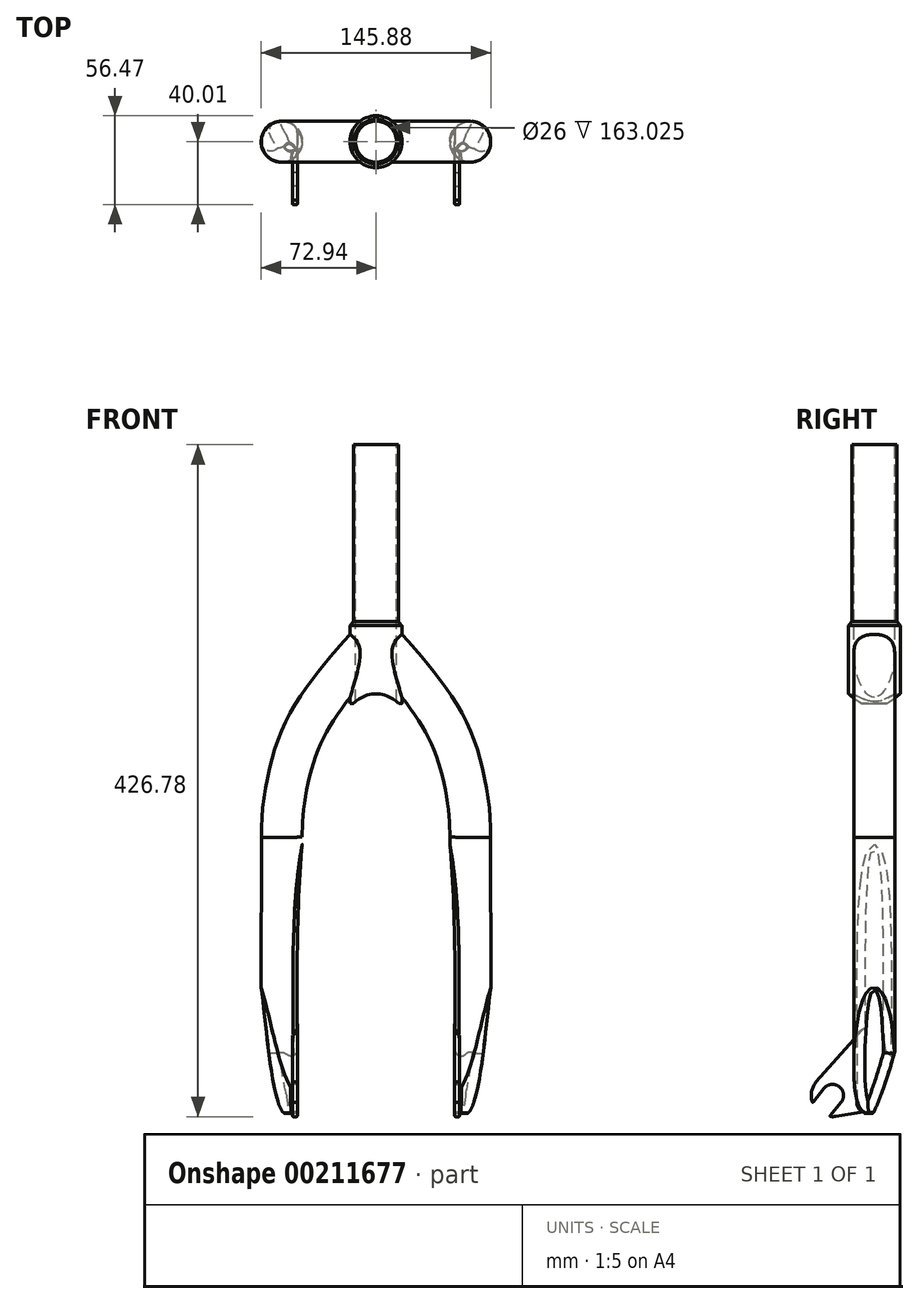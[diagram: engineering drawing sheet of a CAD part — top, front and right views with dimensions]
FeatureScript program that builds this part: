
annotation { "Feature Type Name" : "Feature", "Feature Type Description" : "" }
export const myFeature = defineFeature(function(context is Context, id is Id, definition is map)
    precondition{}
    {
        {
            var Q0;
            Q0=qCreatedBy(makeId("Top.planeOp"),FACE);
            var sketch = newSketch(context, id + "F0", { "sketchPlane" : qUnion([Q0])});
            skCircle(sketch, "E0", {"center": v(0, 0) * mm, "radius": 14.25 * mm});
            skSolve(sketch);
        }
        {
            var Q0;
            Q0 = qSketchRegion(id + "F0", true);
            extrude(context, id + "F1", {"entities" : qUnion([Q0]), "depth" : 162.4 * mm});
        }
        {
            var Q0;
            Q0=qCreatedBy(makeId("Front.planeOp"),FACE);
            var sketch = newSketch(context, id + "F2", { "sketchPlane" : qUnion([Q0])});
            skLineSegment(sketch, "E1", {"start": v(0, 0) * mm, "end": v(-14.25, 0) * mm});
            skLineSegment(sketch, "E2", {"start": v(-14.25, 0) * mm, "end": v(-16.46, -2.53) * mm});
            skLineSegment(sketch, "E3", {"start": v(0, 0) * mm, "end": v(0, -52) * mm});
            skLineSegment(sketch, "E4", {"start": v(0, -52) * mm, "end": v(-16.46, -52) * mm});
            skLineSegment(sketch, "E5", {"start": v(-16.46, -2.53) * mm, "end": v(-16.46, -52) * mm});
            skSolve(sketch);
        }
        {
            var Q0;
            Q0=makeQuery(id+"F2.imprint","IMPRINT",FACE,{"disambiguationData":[TD([[makeQuery(id+"F2.imprint","IMPRINT",EDGE,{"derivedFrom":sQuery(id+"F2.wireOp",EDGE,"E1")}),1.0]])]});
            var Q1;
            Q1=sQuery(id+"F2.wireOp",EDGE,"E3");
            revolve(context, id + "F3", {"operationType" : NewBodyOperationType.ADD, "entities" : qUnion([Q0]), "axis" : qUnion([Q1]), "revolveType" : RevolveType.FULL});
        }
        {
            var Q0;
            Q0=qCreatedBy(makeId("Front.planeOp"),FACE);
            var sketch = newSketch(context, id + "F4", { "sketchPlane" : qUnion([Q0])});
            skCircle(sketch, "E6", {"center": v(0, -65.82) * mm, "radius": 20 * mm});
            skSolve(sketch);
        }
        {
            var Q0;
            Q0=makeQuery(id+"F4.imprint","IMPRINT",FACE,{"disambiguationData":[TD([[makeQuery(id+"F4.imprint","IMPRINT",EDGE,{"derivedFrom":sQuery(id+"F4.wireOp",EDGE,"E6")}),1.0]])]});
            extrude(context, id + "F5", {"entities" : qUnion([Q0]), "depth" : 19 * mm, "hasSecondDirection" : true, "secondDirectionOppositeDirection" : true, "secondDirectionDepth" : 19.7 * mm});
        }
        {
            var Q0;
            Q0=makeQuery(id+"F5.opExtrude","SWEPT_BODY",BODY,{"disambiguationData":[OSD([sQuery(id+"F4.wireOp",EDGE,"E6")])]});
            var Q1;
            Q1=makeQuery(id+"F1.opExtrude","SWEPT_BODY",BODY,{"disambiguationData":[OSD([sQuery(id+"F0.wireOp",EDGE,"E0")])]});
            booleanBodies(context, id + "F6", {"operationType" : BooleanOperationType.SUBTRACTION, "tools" : qUnion([Q0]), "targets" : qUnion([Q1])});
        }
        {
            var Q0;
            Q0=qCreatedBy(makeId("Top.planeOp"),FACE);
            cPlane(context, id + "F7", {"entities" : qUnion([Q0]), "cplaneType" : CPlaneType.OFFSET, "offset" : 315 * mm, "oppositeDirection" : true, "width" : 150 * mm, "height" : 150 * mm});
        }
        {
            var Q0;
            Q0=qCreatedBy(id+"F7.planeOp",FACE);
            var sketch = newSketch(context, id + "F8", { "sketchPlane" : qUnion([Q0])});
            skCircle(sketch, "E7", {"center": v(-60, 0) * mm, "radius": 13 * mm});
            skLineSegment(sketch, "E8", {"start": v(0, 0) * mm, "end": v(-60, 0) * mm});
            skSolve(sketch);
        }
        {
            var Q0;
            Q0=qCreatedBy(makeId("Front.planeOp"),FACE);
            var sketch = newSketch(context, id + "F9", { "sketchPlane" : qUnion([Q0])});
            skPoint(sketch, "E9.0", {"position": v(-60, -315) * mm});
            skFitSpline(sketch, "E10", {"points": [v(0, -8.9) * mm, v(-47.93, -74.33) * mm, v(-59.86, -136.93) * mm], "startDerivative": vector(-113.13, -130.43) * mm, "endDerivative": vector(1.5, -99.2) * mm});
            skLineSegment(sketch, "E11", {"start": v(-60, -315) * mm, "end": v(-59.86, -136.93) * mm});
            skSolve(sketch);
        }
        {
            var Q0;
            Q0=makeQuery(id+"F8.imprint","IMPRINT",FACE,{"disambiguationData":[TD([[makeQuery(id+"F8.imprint","IMPRINT",EDGE,{"derivedFrom":sQuery(id+"F8.wireOp",EDGE,"E7")}),1.0]])]});
            var Q1;
            Q1=sQuery(id+"F9.wireOp",EDGE,"E11");
            var Q2;
            Q2=sQuery(id+"F9.wireOp",EDGE,"E10");
            sweep(context, id + "F10", {"operationType" : NewBodyOperationType.ADD, "profiles" : qUnion([Q0]), "path" : qUnion([Q1, Q2])});
        }
        {
            var Q0;
            Q0=makeQuery(id+"F1.opExtrude","SWEPT_BODY",BODY,{"disambiguationData":[OSD([sQuery(id+"F0.wireOp",EDGE,"E0")])]});
            var Q1;
            Q1=qCreatedBy(makeId("Right.planeOp"),FACE);
            mirror(context, id + "F11", {"operationType" : NewBodyOperationType.ADD, "entities" : qUnion([Q0]), "mirrorPlane" : qUnion([Q1])});
        }
        {
            var Q0;
            Q0=makeQuery(id+"F1.opExtrude","CAP_FACE",FACE,{"disambiguationData":[OSD([sQuery(id+"F0.wireOp",EDGE,"E0")])],"isStart":false});
            var sketch = newSketch(context, id + "F12", { "sketchPlane" : qUnion([Q0])});
            skCircle(sketch, "E12", {"center": v(0, 0) * mm, "radius": 13 * mm});
            skSolve(sketch);
        }
        {
            var Q0;
            Q0=makeQuery(id+"F12.imprint","IMPRINT",FACE,{"disambiguationData":[TD([[makeQuery(id+"F12.imprint","IMPRINT",EDGE,{"derivedFrom":sQuery(id+"F12.wireOp",EDGE,"E12")}),1.0]])]});
            var Q1;
            Q1=sQuery(id+"F12.wireOp",EDGE,"E12");
            extrude(context, id + "F13", {"entities" : qUnion([Q0]), "operationType" : NewBodyOperationType.REMOVE, "surfaceEntities" : qUnion([Q1]), "oppositeDirection" : true, "depth" : 243.5 * mm});
        }
        {
            var Q0;
            Q0=makeQuery(id+"F10.boolean.opBoolean","INTERSECT",EDGE,{"derivedFrom":[makeQuery(id+"F3.opRevolve","SWEPT_FACE",FACE,{"disambiguationData":[OSD([sQuery(id+"F2.wireOp",EDGE,"E5")])]}),makeQuery(id+"F10.opSweep","SWEPT_FACE",FACE,{"disambiguationData":[OSD([sQuery(id+"F8.wireOp",EDGE,"E7"),sQuery(id+"F9.wireOp",EDGE,"E10")])]})]});
            var Q1;
            Q1=makeQuery(id+"F11.opPattern","COPY",EDGE,{"derivedFrom":makeQuery(id+"F10.boolean.opBoolean","INTERSECT",EDGE,{"derivedFrom":[makeQuery(id+"F3.opRevolve","SWEPT_FACE",FACE,{"disambiguationData":[OSD([sQuery(id+"F2.wireOp",EDGE,"E5")])]}),makeQuery(id+"F10.opSweep","SWEPT_FACE",FACE,{"disambiguationData":[OSD([sQuery(id+"F8.wireOp",EDGE,"E7"),sQuery(id+"F9.wireOp",EDGE,"E10")])]})]}),"instanceName":"1"});
            fillet(context, id + "F14", {"entities" : qUnion([Q0, Q1]), "radius" : 1 * mm, "tangentPropagation" : true, "allowEdgeOverflow" : false});
        }
        {
            var Q0;
            Q0=qCreatedBy(makeId("Right.planeOp"),FACE);
            var sketch = newSketch(context, id + "F15", { "sketchPlane" : qUnion([Q0])});
            skArc(sketch, "E13", {"start": v(-37, -292.37) * mm, "mid": v(-38.2, -307.64) * mm, "end": v(-24.36, -314.2) * mm});
            skLineSegment(sketch, "E14", {"start": v(0, -250.54) * mm, "end": v(0, -310.31) * mm});
            skLineSegment(sketch, "E15", {"start": v(-24.36, -314.2) * mm, "end": v(0, -310.31) * mm});
            skLineSegment(sketch, "E16", {"start": v(-37, -292.37) * mm, "end": v(0, -250.54) * mm});
            skSolve(sketch);
        }
        {
            var Q0;
            Q0=makeQuery(id+"F15.imprint","IMPRINT",FACE,{"disambiguationData":[TD([[makeQuery(id+"F15.imprint","IMPRINT",EDGE,{"derivedFrom":sQuery(id+"F15.wireOp",EDGE,"E13")}),1.0]])]});
            extrude(context, id + "F16", {"entities" : qUnion([Q0]), "operationType" : NewBodyOperationType.ADD, "depth" : 53 * mm, "hasSecondDirection" : true, "secondDirectionOppositeDirection" : true, "secondDirectionDepth" : 53 * mm});
        }
        {
            var Q0;
            Q0=qCreatedBy(makeId("Right.planeOp"),FACE);
            var sketch = newSketch(context, id + "F17", { "sketchPlane" : qUnion([Q0])});
            skLineSegment(sketch, "E17.0.1", {"start": v(-10.96, -312.06) * mm, "end": v(-24.36, -314.2) * mm});
            skArc(sketch, "E17.0.2", {"start": v(-24.36, -314.2) * mm, "mid": v(-38.2, -307.64) * mm, "end": v(-37, -292.37) * mm});
            skLineSegment(sketch, "E17.0.3", {"start": v(-37, -292.37) * mm, "end": v(-10.98, -262.96) * mm});
            skLineSegment(sketch, "E18", {"start": v(-37, -292.37) * mm, "end": v(17.67, -230.56) * mm});
            skLineSegment(sketch, "E19", {"start": v(-24.36, -314.2) * mm, "end": v(43.27, -303.4) * mm});
            skLineSegment(sketch, "E20", {"start": v(43.27, -303.4) * mm, "end": v(17.67, -230.56) * mm});
            skSolve(sketch);
        }
        {
            var Q0;
            Q0 = qSketchRegion(id + "F17", true);
            extrude(context, id + "F18", {"entities" : qUnion([Q0]), "operationType" : NewBodyOperationType.REMOVE, "oppositeDirection" : true, "depth" : 50 * mm, "hasSecondDirection" : true, "secondDirectionOppositeDirection" : false, "secondDirectionDepth" : 50 * mm});
        }
        {
            var Q0;
            Q0=makeQuery(id+"F10.opSweep","CAP_FACE",FACE,{"disambiguationData":[OSD([sQuery(id+"F8.wireOp",EDGE,"E7"),sQuery(id+"F9.wireOp",VERTEX,"E11.start")])],"isStart":true});
            var sketch = newSketch(context, id + "F19", { "sketchPlane" : qUnion([Q0])});
            skCircle(sketch, "E21", {"center": v(-60, 0) * mm, "radius": 13.5 * mm});
            skSolve(sketch);
        }
        {
            var Q0;
            Q0 = qSketchRegion(id + "F19", true);
            extrude(context, id + "F20", {"entities" : qUnion([Q0]), "operationType" : NewBodyOperationType.REMOVE, "oppositeDirection" : true, "depth" : 2.8 * mm});
        }
        {
            var Q0;
            Q0=makeQuery(id+"F1.opExtrude","SWEPT_BODY",BODY,{"disambiguationData":[OSD([sQuery(id+"F0.wireOp",EDGE,"E0")])]});
            var Q1;
            Q1=qCreatedBy(makeId("Right.planeOp"),FACE);
            mirror(context, id + "F21", {"operationType" : NewBodyOperationType.INTERSECT, "entities" : qUnion([Q0]), "mirrorPlane" : qUnion([Q1])});
        }
        {
            var Q0;
            Q0=qCreatedBy(makeId("Front.planeOp"),FACE);
            var sketch = newSketch(context, id + "F22", { "sketchPlane" : qUnion([Q0])});
            skFitSpline(sketch, "E22.0", {"points": [v(-47, -312.2) * mm, v(-55.66, -312.2) * mm, v(-64.33, -312.2) * mm, v(-73, -312.2) * mm]});
            skFitSpline(sketch, "E23", {"points": [v(-54.32, -320.93) * mm, v(-67.6, -277.9) * mm, v(-79.55, -201.3) * mm], "startDerivative": vector(-50.6, 60.55) * mm, "endDerivative": vector(-36.25, 107.2) * mm});
            skLineSegment(sketch, "E24", {"start": v(-54.32, -320.93) * mm, "end": v(-140.96, -341.08) * mm});
            skLineSegment(sketch, "E25", {"start": v(-140.96, -341.08) * mm, "end": v(-79.55, -201.3) * mm});
            skSolve(sketch);
        }
        {
            var Q0;
            {var subQ0=sQuery(id+"F22.wireOp",EDGE,"E24");Q0=makeQuery(id+"F22.imprint","IMPRINT",FACE,{"disambiguationData":[TD([[makeQuery(id+"F22.imprint","IMPRINT",EDGE,{"derivedFrom":subQ0}),-1.0]])]});}
            extrude(context, id + "F23", {"entities" : qUnion([Q0]), "operationType" : NewBodyOperationType.REMOVE, "oppositeDirection" : true, "depth" : 25 * mm, "hasSecondDirection" : true, "secondDirectionOppositeDirection" : false, "secondDirectionDepth" : 76.3 * mm});
        }
        {
            var Q0;
            Q0=qCreatedBy(makeId("Right.planeOp"),FACE);
            var sketch = newSketch(context, id + "F24", { "sketchPlane" : qUnion([Q0])});
            skFitSpline(sketch, "E26", {"points": [v(20.3, -244.57) * mm, v(11.96, -277) * mm, v(-12.12, -335.12) * mm, v(-46.63, -372.17) * mm], "startDerivative": vector(-24.7, -105.88) * mm, "endDerivative": vector(-108.24, -94.52) * mm});
            skLineSegment(sketch, "E27", {"start": v(20.3, -244.57) * mm, "end": v(48.1, -363.6) * mm});
            skLineSegment(sketch, "E28", {"start": v(48.1, -363.6) * mm, "end": v(-46.63, -372.17) * mm});
            skSolve(sketch);
        }
        {
            var Q0;
            Q0=makeQuery(id+"F24.imprint","IMPRINT",FACE,{"disambiguationData":[TD([[makeQuery(id+"F24.imprint","IMPRINT",EDGE,{"derivedFrom":sQuery(id+"F24.wireOp",EDGE,"E26")}),1.0]])]});
            extrude(context, id + "F25", {"entities" : qUnion([Q0]), "operationType" : NewBodyOperationType.REMOVE, "oppositeDirection" : true, "depth" : 92.1 * mm});
        }
        {
            var Q0;
            Q0=qCreatedBy(makeId("Front.planeOp"),FACE);
            var sketch = newSketch(context, id + "F26", { "sketchPlane" : qUnion([Q0])});
            skPoint(sketch, "E29.0", {"position": v(-50, -314.2) * mm});
            skLineSegment(sketch, "E30", {"start": v(-50, -314.2) * mm, "end": v(-50, -345.46) * mm});
            skLineSegment(sketch, "E31", {"start": v(-50, -314.2) * mm, "end": v(-50, -258.24) * mm});
            skFitSpline(sketch, "E32", {"points": [v(-50, -258.24) * mm, v(-50, -209.78) * mm, v(-46.14, -135.31) * mm, v(-36.08, -84.53) * mm], "startDerivative": vector(-1.03, 147.16) * mm, "endDerivative": vector(36.5, 149.52) * mm});
            skLineSegment(sketch, "E33", {"start": v(-36.08, -84.53) * mm, "end": v(-4.07, -180.95) * mm});
            skLineSegment(sketch, "E34", {"start": v(-4.07, -180.95) * mm, "end": v(-50, -345.46) * mm});
            skSolve(sketch);
        }
        {
            var Q0;
            Q0=makeQuery(id+"F26.imprint","IMPRINT",FACE,{"disambiguationData":[TD([[makeQuery(id+"F26.imprint","IMPRINT",EDGE,{"derivedFrom":sQuery(id+"F26.wireOp",EDGE,"E30")}),1.0]])]});
            extrude(context, id + "F27", {"entities" : qUnion([Q0]), "operationType" : NewBodyOperationType.REMOVE, "oppositeDirection" : true, "depth" : 164.6 * mm, "hasSecondDirection" : true, "secondDirectionOppositeDirection" : false, "secondDirectionDepth" : 151.8 * mm});
        }
        {
            var Q0;
            Q0=makeQuery(id+"F27.boolean.opBoolean","INTERSECT",EDGE,{"derivedFrom":[makeQuery(id+"F10.opSweep","SWEPT_FACE",FACE,{"disambiguationData":[OSD([sQuery(id+"F8.wireOp",EDGE,"E7"),sQuery(id+"F9.wireOp",EDGE,"E11")])]}),makeQuery(id+"F27.opExtrude","SWEPT_FACE",FACE,{"disambiguationData":[OSD([sQuery(id+"F26.wireOp",EDGE,"E32")])]})]});
            fillet(context, id + "F28", {"entities" : qUnion([Q0]), "radius" : 6 * mm, "tangentPropagation" : true, "allowEdgeOverflow" : false});
        }
        {
            var Q0;
            Q0=makeQuery(id+"F23.boolean.opBoolean","INTERSECT",EDGE,{"derivedFrom":[makeQuery(id+"F10.opSweep","SWEPT_FACE",FACE,{"disambiguationData":[OSD([sQuery(id+"F8.wireOp",EDGE,"E7"),sQuery(id+"F9.wireOp",EDGE,"E11")])]}),makeQuery(id+"F23.opExtrude","SWEPT_FACE",FACE,{"disambiguationData":[OSD([sQuery(id+"F22.wireOp",EDGE,"E23")])]})]});
            var Q1;
            Q1=makeQuery(id+"F25.boolean.opBoolean","INTERSECT",EDGE,{"derivedFrom":[makeQuery(id+"F23.boolean.opBoolean","COPY",FACE,{"derivedFrom":makeQuery(id+"F23.opExtrude","SWEPT_FACE",FACE,{"disambiguationData":[OSD([sQuery(id+"F22.wireOp",EDGE,"E23")])]})}),makeQuery(id+"F25.opExtrude","SWEPT_FACE",FACE,{"disambiguationData":[OSD([sQuery(id+"F24.wireOp",EDGE,"E26")])]})]});
            var Q2;
            Q2=makeQuery(id+"F27.boolean.opBoolean","INTERSECT",EDGE,{"derivedFrom":[makeQuery(id+"F25.boolean.opBoolean","COPY",FACE,{"derivedFrom":makeQuery(id+"F25.opExtrude","SWEPT_FACE",FACE,{"disambiguationData":[OSD([sQuery(id+"F24.wireOp",EDGE,"E26")])]})}),makeQuery(id+"F27.opExtrude","SWEPT_FACE",FACE,{"disambiguationData":[OSD([sQuery(id+"F26.wireOp",EDGE,"E30"),sQuery(id+"F26.wireOp",EDGE,"E31")])]})]});
            fillet(context, id + "F29", {"entities" : qUnion([Q0, Q1, Q2]), "radius" : 7 * mm, "tangentPropagation" : true, "allowEdgeOverflow" : false});
        }
        {
            var Q0;
            Q0=makeQuery(id+"F16.opExtrude","CAP_EDGE",EDGE,{"disambiguationData":[OSD([sQuery(id+"F15.wireOp",EDGE,"E15")])],"isStart":true});
            var Q1;
            {var subQ0=sQuery(id+"F17.wireOp",EDGE,"E19");Q1=makeQuery(id+"F18.boolean.opBoolean","COPY",EDGE,{"disambiguationData":[TD([makeQuery(id+"F10.opSweep","SWEPT_FACE",FACE,{"disambiguationData":[OSD([sQuery(id+"F8.wireOp",EDGE,"E7"),sQuery(id+"F9.wireOp",EDGE,"E11")])]}),makeQuery(id+"F16.opExtrude","SWEPT_FACE",FACE,{"disambiguationData":[OSD([sQuery(id+"F15.wireOp",EDGE,"E13")])]}),makeQuery(id+"F16.opExtrude","SWEPT_FACE",FACE,{"disambiguationData":[OSD([sQuery(id+"F15.wireOp",EDGE,"E15")])]}),makeQuery(id+"F18.opExtrude","CAP_FACE",FACE,{"disambiguationData":[OSD([sQuery(id+"F17.wireOp",EDGE,"E17.0.2"),sQuery(id+"F17.wireOp",EDGE,"E18"),subQ0,sQuery(id+"F17.wireOp",EDGE,"E20")])],"isStart":false}),makeQuery(id+"F18.opExtrude","SWEPT_FACE",FACE,{"disambiguationData":[OSD([subQ0])]})])],"derivedFrom":makeQuery(id+"F18.opExtrude","CAP_EDGE",EDGE,{"disambiguationData":[OSD([subQ0])],"isStart":false})});}
            var Q2;
            Q2=makeQuery(id+"F16.opExtrude","CAP_EDGE",EDGE,{"disambiguationData":[OSD([sQuery(id+"F15.wireOp",EDGE,"E13")])],"isStart":true});
            var Q3;
            Q3=makeQuery(id+"F18.boolean.opBoolean","COPY",EDGE,{"derivedFrom":makeQuery(id+"F18.opExtrude","CAP_EDGE",EDGE,{"disambiguationData":[OSD([sQuery(id+"F17.wireOp",EDGE,"E17.0.2")])],"isStart":false})});
            var Q4;
            Q4=makeQuery(id+"F16.opExtrude","CAP_EDGE",EDGE,{"disambiguationData":[OSD([sQuery(id+"F15.wireOp",EDGE,"E16")])],"isStart":true});
            var Q5;
            {var subQ0=sQuery(id+"F17.wireOp",EDGE,"E18");Q5=makeQuery(id+"F18.boolean.opBoolean","COPY",EDGE,{"disambiguationData":[TD([makeQuery(id+"F10.opSweep","SWEPT_FACE",FACE,{"disambiguationData":[OSD([sQuery(id+"F8.wireOp",EDGE,"E7"),sQuery(id+"F9.wireOp",EDGE,"E11")])]}),makeQuery(id+"F16.opExtrude","SWEPT_FACE",FACE,{"disambiguationData":[OSD([sQuery(id+"F15.wireOp",EDGE,"E13")])]}),makeQuery(id+"F16.opExtrude","SWEPT_FACE",FACE,{"disambiguationData":[OSD([sQuery(id+"F15.wireOp",EDGE,"E16")])]}),makeQuery(id+"F18.opExtrude","CAP_FACE",FACE,{"disambiguationData":[OSD([sQuery(id+"F17.wireOp",EDGE,"E17.0.2"),subQ0,sQuery(id+"F17.wireOp",EDGE,"E19"),sQuery(id+"F17.wireOp",EDGE,"E20")])],"isStart":false}),makeQuery(id+"F18.opExtrude","SWEPT_FACE",FACE,{"disambiguationData":[OSD([subQ0])]})])],"derivedFrom":makeQuery(id+"F18.opExtrude","CAP_EDGE",EDGE,{"disambiguationData":[OSD([subQ0])],"isStart":false})});}
            fillet(context, id + "F30", {"entities" : qUnion([Q0, Q1, Q2, Q3, Q4, Q5]), "radius" : .5 * mm, "tangentPropagation" : true, "allowEdgeOverflow" : false});
        }
        {
            var Q0;
            Q0=makeQuery(id+"F29.opFillet","BLEND_EDGE",EDGE,{"disambiguationData":[OD(1.0)],"blendedFrom":[makeQuery(id+"F27.boolean.opBoolean","INTERSECT",EDGE,{"derivedFrom":[makeQuery(id+"F25.boolean.opBoolean","COPY",FACE,{"derivedFrom":makeQuery(id+"F25.opExtrude","SWEPT_FACE",FACE,{"disambiguationData":[OSD([sQuery(id+"F24.wireOp",EDGE,"E26")])]})}),makeQuery(id+"F27.opExtrude","SWEPT_FACE",FACE,{"disambiguationData":[OSD([sQuery(id+"F26.wireOp",EDGE,"E30"),sQuery(id+"F26.wireOp",EDGE,"E31")])]})]}),makeQuery(id+"F20.boolean.opBoolean","COPY",FACE,{"derivedFrom":makeQuery(id+"F20.opExtrude","CAP_FACE",FACE,{"disambiguationData":[OSD([sQuery(id+"F19.wireOp",EDGE,"E21")])],"isStart":false})})],"blendedInto":[makeQuery(id+"F20.boolean.opBoolean","COPY",FACE,{"derivedFrom":makeQuery(id+"F20.opExtrude","CAP_FACE",FACE,{"disambiguationData":[OSD([sQuery(id+"F19.wireOp",EDGE,"E21")])],"isStart":false})})]});
            var Q1;
            Q1=makeQuery(id+"F29.opFillet","BLEND_EDGE",EDGE,{"disambiguationData":[OD(0.0)],"blendedFrom":[makeQuery(id+"F27.boolean.opBoolean","INTERSECT",EDGE,{"derivedFrom":[makeQuery(id+"F25.boolean.opBoolean","COPY",FACE,{"derivedFrom":makeQuery(id+"F25.opExtrude","SWEPT_FACE",FACE,{"disambiguationData":[OSD([sQuery(id+"F24.wireOp",EDGE,"E26")])]})}),makeQuery(id+"F27.opExtrude","SWEPT_FACE",FACE,{"disambiguationData":[OSD([sQuery(id+"F26.wireOp",EDGE,"E30"),sQuery(id+"F26.wireOp",EDGE,"E31")])]})]}),makeQuery(id+"F20.boolean.opBoolean","COPY",FACE,{"derivedFrom":makeQuery(id+"F20.opExtrude","CAP_FACE",FACE,{"disambiguationData":[OSD([sQuery(id+"F19.wireOp",EDGE,"E21")])],"isStart":false})})],"blendedInto":[makeQuery(id+"F20.boolean.opBoolean","COPY",FACE,{"derivedFrom":makeQuery(id+"F20.opExtrude","CAP_FACE",FACE,{"disambiguationData":[OSD([sQuery(id+"F19.wireOp",EDGE,"E21")])],"isStart":false})})]});
            var Q2;
            Q2=makeQuery(id+"F29.opFillet","BLEND_EDGE",EDGE,{"disambiguationData":[OD(1.0)],"blendedFrom":[makeQuery(id+"F25.boolean.opBoolean","INTERSECT",EDGE,{"derivedFrom":[makeQuery(id+"F23.boolean.opBoolean","COPY",FACE,{"derivedFrom":makeQuery(id+"F23.opExtrude","SWEPT_FACE",FACE,{"disambiguationData":[OSD([sQuery(id+"F22.wireOp",EDGE,"E23")])]})}),makeQuery(id+"F25.opExtrude","SWEPT_FACE",FACE,{"disambiguationData":[OSD([sQuery(id+"F24.wireOp",EDGE,"E26")])]})]}),makeQuery(id+"F20.boolean.opBoolean","COPY",FACE,{"derivedFrom":makeQuery(id+"F20.opExtrude","CAP_FACE",FACE,{"disambiguationData":[OSD([sQuery(id+"F19.wireOp",EDGE,"E21")])],"isStart":false})})],"blendedInto":[makeQuery(id+"F20.boolean.opBoolean","COPY",FACE,{"derivedFrom":makeQuery(id+"F20.opExtrude","CAP_FACE",FACE,{"disambiguationData":[OSD([sQuery(id+"F19.wireOp",EDGE,"E21")])],"isStart":false})})]});
            var Q3;
            Q3=makeQuery(id+"F29.opFillet","BLEND_EDGE",EDGE,{"disambiguationData":[OD(0.0)],"blendedFrom":[makeQuery(id+"F25.boolean.opBoolean","INTERSECT",EDGE,{"derivedFrom":[makeQuery(id+"F23.boolean.opBoolean","COPY",FACE,{"derivedFrom":makeQuery(id+"F23.opExtrude","SWEPT_FACE",FACE,{"disambiguationData":[OSD([sQuery(id+"F22.wireOp",EDGE,"E23")])]})}),makeQuery(id+"F25.opExtrude","SWEPT_FACE",FACE,{"disambiguationData":[OSD([sQuery(id+"F24.wireOp",EDGE,"E26")])]})]}),makeQuery(id+"F20.boolean.opBoolean","COPY",FACE,{"derivedFrom":makeQuery(id+"F20.opExtrude","CAP_FACE",FACE,{"disambiguationData":[OSD([sQuery(id+"F19.wireOp",EDGE,"E21")])],"isStart":false})})],"blendedInto":[makeQuery(id+"F20.boolean.opBoolean","COPY",FACE,{"derivedFrom":makeQuery(id+"F20.opExtrude","CAP_FACE",FACE,{"disambiguationData":[OSD([sQuery(id+"F19.wireOp",EDGE,"E21")])],"isStart":false})})]});
            var Q4;
            Q4=makeQuery(id+"F29.opFillet","BLEND_EDGE",EDGE,{"blendedFrom":[makeQuery(id+"F23.boolean.opBoolean","INTERSECT",EDGE,{"derivedFrom":[makeQuery(id+"F10.opSweep","SWEPT_FACE",FACE,{"disambiguationData":[OSD([sQuery(id+"F8.wireOp",EDGE,"E7"),sQuery(id+"F9.wireOp",EDGE,"E11")])]}),makeQuery(id+"F23.opExtrude","SWEPT_FACE",FACE,{"disambiguationData":[OSD([sQuery(id+"F22.wireOp",EDGE,"E23")])]})]}),makeQuery(id+"F20.boolean.opBoolean","COPY",FACE,{"derivedFrom":makeQuery(id+"F20.opExtrude","CAP_FACE",FACE,{"disambiguationData":[OSD([sQuery(id+"F19.wireOp",EDGE,"E21")])],"isStart":false})})],"blendedInto":[makeQuery(id+"F20.boolean.opBoolean","COPY",FACE,{"derivedFrom":makeQuery(id+"F20.opExtrude","CAP_FACE",FACE,{"disambiguationData":[OSD([sQuery(id+"F19.wireOp",EDGE,"E21")])],"isStart":false})})]});
            var Q5;
            Q5=makeQuery(id+"F20.boolean.opBoolean","INTERSECT",EDGE,{"derivedFrom":[makeQuery(id+"F10.opSweep","SWEPT_FACE",FACE,{"disambiguationData":[OSD([sQuery(id+"F8.wireOp",EDGE,"E7"),sQuery(id+"F9.wireOp",EDGE,"E11")])]}),makeQuery(id+"F20.opExtrude","CAP_FACE",FACE,{"disambiguationData":[OSD([sQuery(id+"F19.wireOp",EDGE,"E21")])],"isStart":false})]});
            var Q6;
            Q6=makeQuery(id+"F27.boolean.opBoolean","INTERSECT",EDGE,{"derivedFrom":[makeQuery(id+"F20.boolean.opBoolean","COPY",FACE,{"derivedFrom":makeQuery(id+"F20.opExtrude","CAP_FACE",FACE,{"disambiguationData":[OSD([sQuery(id+"F19.wireOp",EDGE,"E21")])],"isStart":false})}),makeQuery(id+"F27.opExtrude","SWEPT_FACE",FACE,{"disambiguationData":[OSD([sQuery(id+"F26.wireOp",EDGE,"E30"),sQuery(id+"F26.wireOp",EDGE,"E31")])]})]});
            fillet(context, id + "F31", {"entities" : qUnion([Q0, Q1, Q2, Q3, Q4, Q5, Q6]), "radius" : 1 * mm, "tangentPropagation" : true, "allowEdgeOverflow" : false});
        }
        {
            var Q0;
            Q0=makeQuery(id+"F16.boolean.opBoolean","INTERSECT",EDGE,{"derivedFrom":[makeQuery(id+"F10.opSweep","SWEPT_FACE",FACE,{"disambiguationData":[OSD([sQuery(id+"F8.wireOp",EDGE,"E7"),sQuery(id+"F9.wireOp",EDGE,"E11")])]}),makeQuery(id+"F16.opExtrude","CAP_FACE",FACE,{"disambiguationData":[OSD([sQuery(id+"F15.wireOp",EDGE,"E13"),sQuery(id+"F15.wireOp",EDGE,"E14"),sQuery(id+"F15.wireOp",EDGE,"E15"),sQuery(id+"F15.wireOp",EDGE,"E16")])],"isStart":true})]});
            fillet(context, id + "F32", {"entities" : qUnion([Q0]), "radius" : 1 * mm, "tangentPropagation" : true, "allowEdgeOverflow" : false});
        }
        {
            var Q0;
            Q0=makeQuery(id+"F1.opExtrude","SWEPT_BODY",BODY,{"disambiguationData":[OSD([sQuery(id+"F0.wireOp",EDGE,"E0")])]});
            var Q1;
            Q1=qCreatedBy(makeId("Right.planeOp"),FACE);
            mirror(context, id + "F33", {"operationType" : NewBodyOperationType.INTERSECT, "entities" : qUnion([Q0]), "mirrorPlane" : qUnion([Q1])});
        }
        {
            var Q0;
            {var subQ0=sQuery(id+"F15.wireOp",EDGE,"E16");var subQ1=sQuery(id+"F15.wireOp",EDGE,"E15");var subQ2=sQuery(id+"F15.wireOp",EDGE,"E14");var subQ3=sQuery(id+"F15.wireOp",EDGE,"E13");Q0=makeQuery(id+"F33.boolean.opBoolean","MERGE",FACE,{"derivedFrom":[makeQuery(id+"F16.opExtrude","CAP_FACE",FACE,{"disambiguationData":[OSD([subQ3,subQ2,subQ1,subQ0])],"isStart":true}),makeQuery(id+"F33.boolean.toolComplement.opBoolean","COPY",FACE,{"derivedFrom":makeQuery(id+"F33.opPattern","COPY",FACE,{"derivedFrom":makeQuery(id+"F16.opExtrude","CAP_FACE",FACE,{"disambiguationData":[OSD([subQ3,subQ2,subQ1,subQ0])],"isStart":false}),"instanceName":"1"})})]});}
            var sketch = newSketch(context, id + "F34", { "sketchPlane" : qUnion([Q0])});
            skLineSegment(sketch, "E35", {"start": v(21.08, -305.29) * mm, "end": v(30.46, -316.86) * mm});
            skLineSegment(sketch, "E36", {"start": v(30.46, -316.86) * mm, "end": v(41.34, -308.04) * mm});
            skArc(sketch, "E37", {"start": v(21.08, -305.29) * mm, "mid": v(22.1, -295.44) * mm, "end": v(31.95, -296.47) * mm});
            skLineSegment(sketch, "E38", {"start": v(41.34, -308.04) * mm, "end": v(31.95, -296.47) * mm});
            skSolve(sketch);
        }
        {
            var Q0;
            Q0 = qSketchRegion(id + "F34", true);
            extrude(context, id + "F35", {"entities" : qUnion([Q0]), "operationType" : NewBodyOperationType.REMOVE, "oppositeDirection" : true, "depth" : 25 * mm});
        }
        {
            var Q0;
            {var subQ0=sQuery(id+"F15.wireOp",EDGE,"E16");var subQ1=sQuery(id+"F15.wireOp",EDGE,"E15");var subQ2=sQuery(id+"F15.wireOp",EDGE,"E13");Q0=makeQuery(id+"F35.boolean.opBoolean","INTERSECT",EDGE,{"derivedFrom":[makeQuery(id+"F18.boolean.opBoolean","SPLIT",FACE,{"disambiguationData":[TD([makeQuery(id+"F16.opExtrude","CAP_FACE",FACE,{"disambiguationData":[OSD([subQ2,sQuery(id+"F15.wireOp",EDGE,"E14"),subQ1,subQ0])],"isStart":true})])],"derivedFrom":makeQuery(id+"F16.opExtrude","SWEPT_FACE",FACE,{"disambiguationData":[OSD([subQ2])]})}),makeQuery(id+"F35.opExtrude","SWEPT_FACE",FACE,{"disambiguationData":[OSD([sQuery(id+"F34.wireOp",EDGE,"E38")])]})]});}
            fillet(context, id + "F36", {"entities" : qUnion([Q0]), "radius" : .25 * mm, "tangentPropagation" : true, "allowEdgeOverflow" : false});
        }
        {
            var Q0;
            Q0=makeQuery(id+"F1.opExtrude","SWEPT_BODY",BODY,{"disambiguationData":[OSD([sQuery(id+"F0.wireOp",EDGE,"E0")])]});
            var Q1;
            Q1=qCreatedBy(makeId("Right.planeOp"),FACE);
            mirror(context, id + "F37", {"operationType" : NewBodyOperationType.INTERSECT, "entities" : qUnion([Q0]), "mirrorPlane" : qUnion([Q1])});
        }
        {
            var Q0;
            Q0=makeQuery(id+"F1.opExtrude","CAP_FACE",FACE,{"disambiguationData":[OSD([sQuery(id+"F0.wireOp",EDGE,"E0")])],"isStart":false});
            var sketch = newSketch(context, id + "F38", { "sketchPlane" : qUnion([Q0])});
            skCircle(sketch, "E39.0", {"center": v(0, 0) * mm, "radius": 13 * mm});
            skCircle(sketch, "E40.0", {"center": v(0, 0) * mm, "radius": 14.25 * mm});
            skSolve(sketch);
        }
        {
            var Q0;
            Q0 = qSketchRegion(id + "F38", true);
            extrude(context, id + "F39", {"entities" : qUnion([Q0]), "operationType" : NewBodyOperationType.REMOVE, "oppositeDirection" : true, "depth" : 50 * mm});
        }
    });
